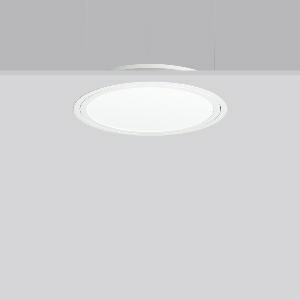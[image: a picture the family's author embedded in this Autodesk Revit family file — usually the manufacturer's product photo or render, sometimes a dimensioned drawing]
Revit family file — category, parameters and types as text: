
# Revit family: triona_round_e_312419_002_2_12_0399
name_source: partatom
category: Lighting Fixtures
units: mm (PartAtom-declared; Revit-internal decimal feet)

## family parameters
Cut with Voids When Loaded = No
Host = Face
Light Source = No
Part Type = Normal
Room Calculation Point = No
Round Connector Dimension = Use Diameter
Shared = No

## types (1)
- TuneableWhite 846 (1 x LED Modul 846, 2450 lm, 4600)
    Apparent Load = 29 VA
    CIE Flux Codes = 48 80 96 100 100
    Color Rendering = 80
    Color Temperature = 4600
    Default Elevation = 1800 mm
    Description = Series: TRIONA round
Decorative round LED recessed surface luminaire. Cover made of sheet steel, powder-coated. Frame made of aluminium, powder-coated. Recessed ring: aluminium extrusion profile, powder coated. Light emission through a diffuser: plastic, opal. Lightguide and diffuser made of non-yellowing plastic (PMMA). Lateral light emission (RZB SIDELITE technology) for above-average homogeneous light distribution. Tunable white versions, dynamically adjustable from 2700 K to 6500 K. Suitable for installation in cavity ceilings. Tool-free mounting system thanks to the rocker arm mechanism (patent pending). Electronic ballast included. Very easy installation thanks to Plug+Play connection. Ideal for use as part of the Human Centric Lighting concept in connection with RZB light management systems. 
Colour: traffic white, matt (RAL 9016)
Diameter: 505 mm
Height: 2 mm
Cut-out diameter: 482 mm
Recess height: 100 mm
Luminaire: recess height: 89 mm
Lamp: LED
Socket: without socket
Colour temperature: 2700K - 6500K
Colour rendering index (CRI): 80
System power: 29 W
Rated luminous flux: 2450 lm
Luminous efficiency: 84 lm/W
System power 2: 29 W
Rated luminous flux 2: 2350 lm
Luminous efficiency 2: 81 lm/W
System power 3: 30 W
Rated luminous flux 3: 2400 lm
Luminous efficiency 3: 80 lm/W
Control gear: Converter, dimmable, DALI
Protection class: I
Type of protection: IP 40
    Height = 0 mm  [stored 0 ft]
    Lamp = 1 x LED Modul 846
    Lamp Light Flux = 2450 lm
    Lamp count = 1
    Length = 505 mm
    Lifetime = 50000 h
    Luminous efficacy = 84 lm/W
    Manufacturer = RZB
    ModVariant = No
    Model = 312419.002.2.12
    Mounting Place = Ceiling
    Mounting Type = Recessed
    Number of Poles = 1
    OnlyDefault = Yes
    Power Factor = 1
    Product Name = TRIONA round E
    Product group = Recessed modular luminaires
    ProductGroupID = 406
    Protection Class = Protection class I
    Protection Degree = IP 20
    RLX_Detail_Level = 1
    RLX_Emergency_Light_Flux = 0 lm
    RLX_Emergency_Type = 0
    RLX_Emergency_Type_DB = No
    RlxData = <blob elided: 31905 chars, md5=6d72d221>
    Socket = socket
    Standby Power = 0 W
    System Light Flux = 2450 lm
    System Power = 29 W
    Type Comments = TuneableWhite 846
    Type Image = 312419.002.12.jpg
    URL = http://relux.com
    VarID = tuneablewhite_846
    Voltage = 230 V
    Voltage Range = 220-240 V
    Weight = 0.00 kg
    Width = 0 mm  [stored 0 ft]

note: [stored X ft] marks values corroborated as IEEE doubles in the binary element streams (Revit-internal decimal feet)

## geometry (parser evidence)
native form markers: Blend x4, Sweep x10
no freeform markers — native parametric forms only
